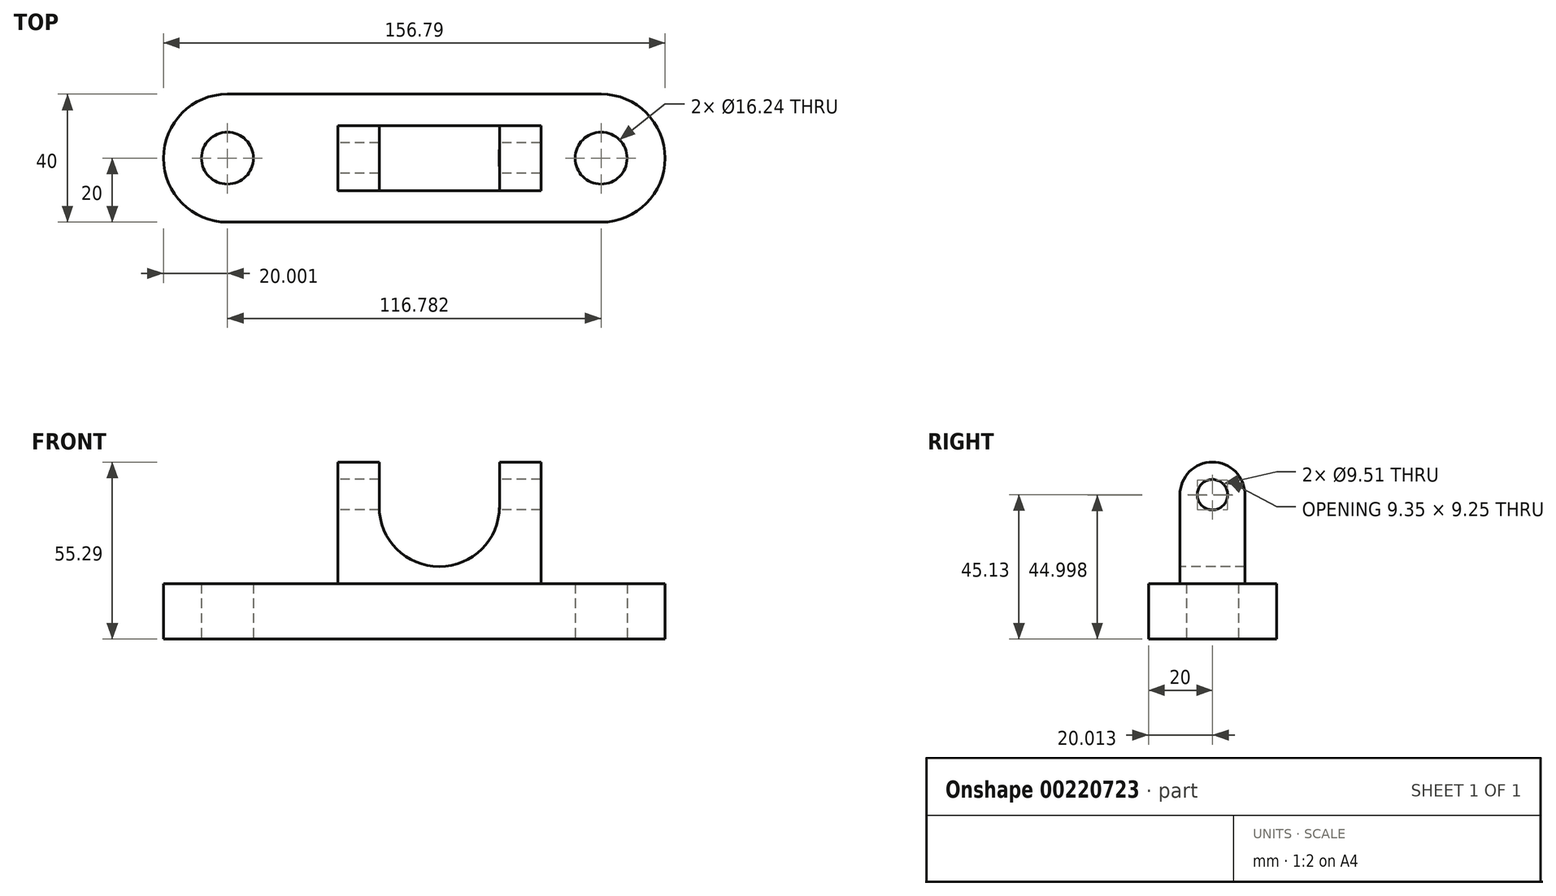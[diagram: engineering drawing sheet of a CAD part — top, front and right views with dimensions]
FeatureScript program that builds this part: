
annotation { "Feature Type Name" : "Feature", "Feature Type Description" : "" }
export const myFeature = defineFeature(function(context is Context, id is Id, definition is map)
    precondition{}
    {
        {
            var Q0;
            Q0=qCreatedBy(makeId("Top.planeOp"),FACE);
            var sketch = newSketch(context, id + "F0", { "sketchPlane" : qUnion([Q0])});
            skArc(sketch, "E0", {"start": v(-66.2, 20) * mm, "mid": v(-86.21, 0) * mm, "end": v(-66.2, -20) * mm});
            skLineSegment(sketch, "E1", {"start": v(-66.2, 20) * mm, "end": v(50.57, 20) * mm});
            skLineSegment(sketch, "E2", {"start": v(-66.2, -20) * mm, "end": v(50.57, -20) * mm});
            skArc(sketch, "E3", {"start": v(50.57, -20) * mm, "mid": v(70.58, 0) * mm, "end": v(50.57, 20) * mm});
            skCircle(sketch, "E4", {"center": v(-66.2, 0) * mm, "radius": 8.12 * mm});
            skCircle(sketch, "E5", {"center": v(50.57, 0) * mm, "radius": 8.12 * mm});
            skSolve(sketch);
        }
        {
            var Q0;
            Q0=makeQuery(id+"F0.imprint","IMPRINT",FACE,{"disambiguationData":[TD([[makeQuery(id+"F0.imprint","IMPRINT",EDGE,{"derivedFrom":sQuery(id+"F0.wireOp",EDGE,"E0")}),1.0]])]});
            extrude(context, id + "F1", {"entities" : qUnion([Q0]), "depth" : 17.27 * mm});
        }
        {
            var Q0;
            Q0=qCreatedBy(makeId("Right.planeOp"),FACE);
            var sketch = newSketch(context, id + "F2", { "sketchPlane" : qUnion([Q0])});
            skLineSegment(sketch, "E6.top", {"start": v(-10.16, 17.33) * mm, "end": v(10.16, 17.33) * mm});
            skLineSegment(sketch, "E6.left", {"start": v(-10.16, 45.13) * mm, "end": v(-10.16, 17.33) * mm});
            skLineSegment(sketch, "E6.right", {"start": v(10.16, 45.13) * mm, "end": v(10.16, 17.33) * mm});
            skArc(sketch, "E7", {"start": v(10.16, 45.13) * mm, "mid": v(0, 55.3) * mm, "end": v(-10.16, 45.13) * mm});
            skCircle(sketch, "E8", {"center": v(0, 45.13) * mm, "radius": 4.76 * mm});
            skSolve(sketch);
        }
        {
            var Q0;
            Q0=makeQuery(id+"F2.imprint","IMPRINT",FACE,{"disambiguationData":[TD([[makeQuery(id+"F2.imprint","IMPRINT",EDGE,{"derivedFrom":sQuery(id+"F2.wireOp",EDGE,"E6.top")}),1.0]])]});
            extrude(context, id + "F3", {"entities" : qUnion([Q0]), "endBound" : BoundingType.SYMMETRIC, "depth" : 63.5 * mm});
        }
        {
            var Q0;
            Q0=qCreatedBy(makeId("Front.planeOp"),FACE);
            var sketch = newSketch(context, id + "F4", { "sketchPlane" : qUnion([Q0])});
            skArc(sketch, "E9", {"start": v(-18.79, 41.4) * mm, "mid": v(0, 22.62) * mm, "end": v(18.79, 41.4) * mm});
            skLineSegment(sketch, "E10", {"start": v(-18.79, 41.4) * mm, "end": v(-18.79, 67.08) * mm});
            skLineSegment(sketch, "E11", {"start": v(18.79, 41.4) * mm, "end": v(18.79, 67.27) * mm});
            skLineSegment(sketch, "E12", {"start": v(-18.79, 67.08) * mm, "end": v(18.79, 67.27) * mm});
            skSolve(sketch);
        }
        {
            var Q0;
            Q0=makeQuery(id+"F4.imprint","IMPRINT",FACE,{"disambiguationData":[TD([[makeQuery(id+"F4.imprint","IMPRINT",EDGE,{"derivedFrom":sQuery(id+"F4.wireOp",EDGE,"E9")}),1.0]])]});
            extrude(context, id + "F5", {"entities" : qUnion([Q0]), "operationType" : NewBodyOperationType.REMOVE, "endBound" : BoundingType.SYMMETRIC, "oppositeDirection" : true, "depth" : 25.4 * mm});
        }
    });
